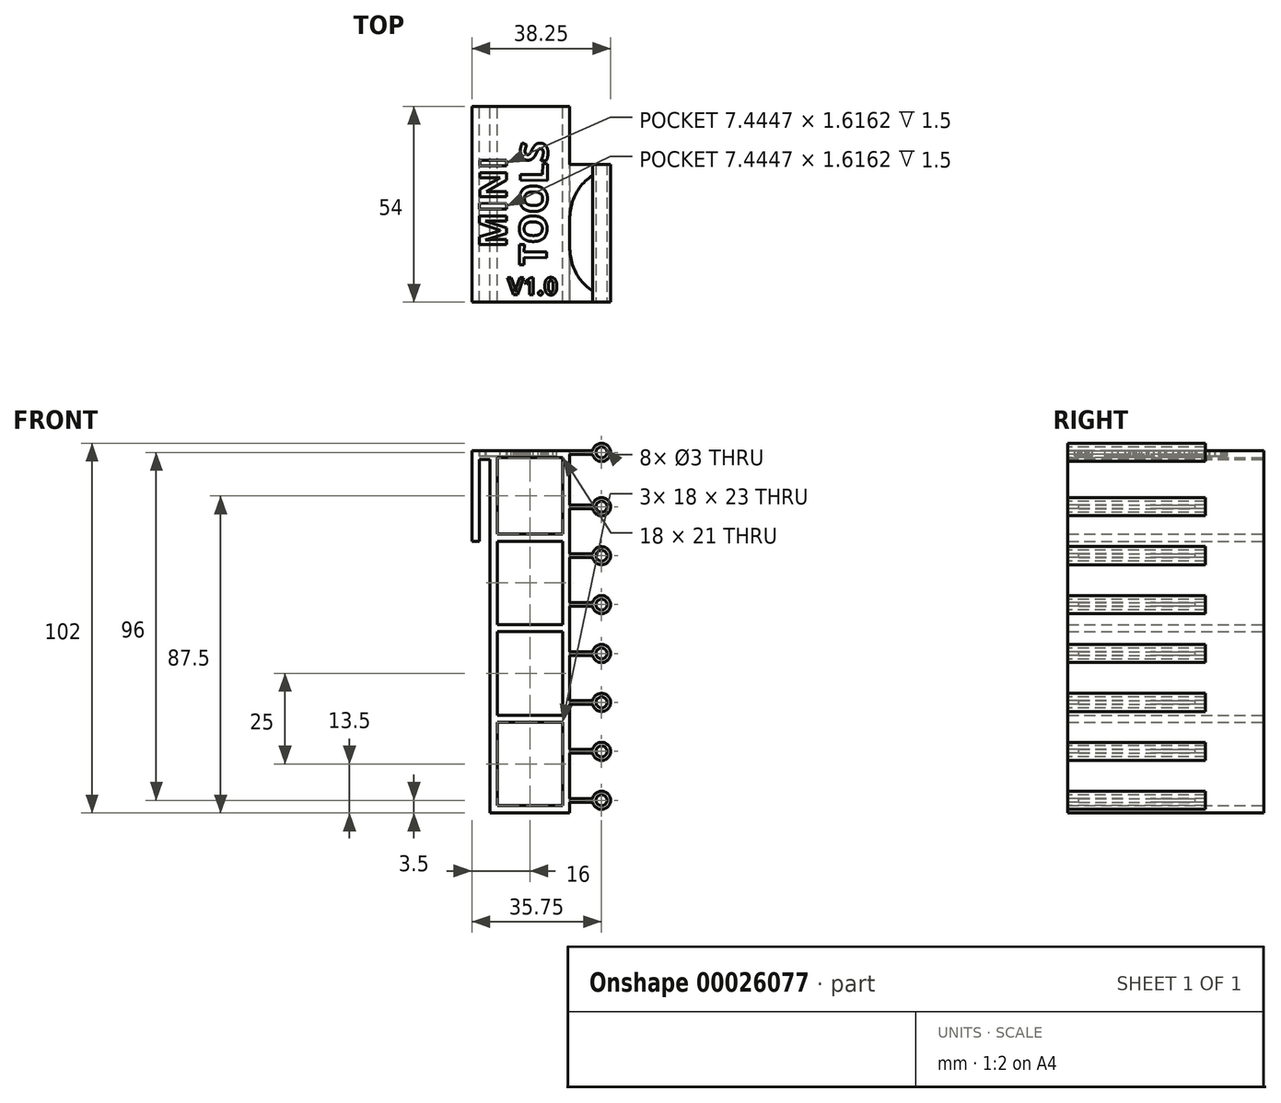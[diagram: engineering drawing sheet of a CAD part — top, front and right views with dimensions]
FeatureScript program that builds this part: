
annotation { "Feature Type Name" : "Feature", "Feature Type Description" : "" }
export const myFeature = defineFeature(function(context is Context, id is Id, definition is map)
    precondition{}
    {
        {
            var Q0;
            Q0=qCreatedBy(makeId("Front.planeOp"),FACE);
            var sketch = newSketch(context, id + "F0", { "sketchPlane" : qUnion([Q0])});
            skLineSegment(sketch, "E0", {"start": v(-37.92, 15.53) * mm, "end": v(-37.92, 40.53) * mm});
            skLineSegment(sketch, "E1", {"start": v(-37.92, 40.53) * mm, "end": v(-35.92, 40.53) * mm});
            skLineSegment(sketch, "E2", {"start": v(-35.92, 40.53) * mm, "end": v(-35.92, 15.53) * mm});
            skLineSegment(sketch, "E3", {"start": v(-35.92, 15.53) * mm, "end": v(-37.92, 15.53) * mm});
            skLineSegment(sketch, "E4", {"start": v(-35.92, 40.53) * mm, "end": v(-32.92, 40.53) * mm});
            skLineSegment(sketch, "E5", {"start": v(-32.92, 40.53) * mm, "end": v(-32.92, -59.47) * mm});
            skLineSegment(sketch, "E6", {"start": v(-32.92, -59.47) * mm, "end": v(-30.92, -59.47) * mm});
            skLineSegment(sketch, "E7", {"start": v(-30.92, -59.47) * mm, "end": v(-30.92, 40.53) * mm});
            skLineSegment(sketch, "E8", {"start": v(-30.92, 40.53) * mm, "end": v(-32.92, 40.53) * mm});
            skLineSegment(sketch, "E9", {"start": v(-30.92, -57.47) * mm, "end": v(-10.92, -57.47) * mm});
            skLineSegment(sketch, "E10", {"start": v(-10.92, -57.47) * mm, "end": v(-10.92, -59.47) * mm});
            skLineSegment(sketch, "E11", {"start": v(-10.92, -59.47) * mm, "end": v(-30.92, -59.47) * mm});
            skLineSegment(sketch, "E12", {"start": v(-35.92, 38.03) * mm, "end": v(-32.92, 38.03) * mm});
            skLineSegment(sketch, "E13", {"start": v(-10.92, -57.47) * mm, "end": v(-10.92, -34.47) * mm});
            skLineSegment(sketch, "E14", {"start": v(-10.92, -34.47) * mm, "end": v(-12.92, -34.47) * mm});
            skLineSegment(sketch, "E15", {"start": v(-12.92, -34.47) * mm, "end": v(-12.92, -57.47) * mm});
            skLineSegment(sketch, "E16.0.1.0", {"start": v(-30.92, -32.47) * mm, "end": v(-10.92, -32.47) * mm});
            skLineSegment(sketch, "E16.0.1.1", {"start": v(-10.92, -34.47) * mm, "end": v(-30.92, -34.47) * mm});
            skLineSegment(sketch, "E16.0.1.2", {"start": v(-10.92, -32.47) * mm, "end": v(-10.92, -34.47) * mm});
            skLineSegment(sketch, "E16.0.1.3", {"start": v(-10.92, -32.47) * mm, "end": v(-10.92, -9.47) * mm});
            skLineSegment(sketch, "E16.0.1.4", {"start": v(-10.92, -9.47) * mm, "end": v(-12.92, -9.47) * mm});
            skLineSegment(sketch, "E16.0.1.5", {"start": v(-12.92, -9.47) * mm, "end": v(-12.92, -32.47) * mm});
            skLineSegment(sketch, "E16.direction1", {"start": v(-30.92, -57.47) * mm, "end": v(-5.92, -57.47) * mm, "construction": true});
            skLineSegment(sketch, "E16.direction2", {"start": v(-30.92, -57.47) * mm, "end": v(-30.92, -32.47) * mm, "construction": true});
            skLineSegment(sketch, "E17.0.0.2", {"start": v(-30.92, -7.47) * mm, "end": v(-10.92, -7.47) * mm});
            skLineSegment(sketch, "E17.3.0.2", {"start": v(-10.92, -9.47) * mm, "end": v(-30.92, -9.47) * mm});
            skLineSegment(sketch, "E17.6.0.2", {"start": v(-10.92, -7.47) * mm, "end": v(-10.92, -9.47) * mm});
            skLineSegment(sketch, "E17.9.0.2", {"start": v(-10.92, -7.47) * mm, "end": v(-10.92, 15.53) * mm});
            skLineSegment(sketch, "E17.12.0.2", {"start": v(-10.92, 15.53) * mm, "end": v(-12.92, 15.53) * mm});
            skLineSegment(sketch, "E17.15.0.2", {"start": v(-12.92, 15.53) * mm, "end": v(-12.92, -7.47) * mm});
            skLineSegment(sketch, "E17.0.0.3", {"start": v(-30.92, 17.53) * mm, "end": v(-10.92, 17.53) * mm});
            skLineSegment(sketch, "E17.3.0.3", {"start": v(-10.92, 15.53) * mm, "end": v(-30.92, 15.53) * mm});
            skLineSegment(sketch, "E17.6.0.3", {"start": v(-10.92, 17.53) * mm, "end": v(-10.92, 15.53) * mm});
            skLineSegment(sketch, "E17.9.0.3", {"start": v(-10.92, 17.53) * mm, "end": v(-10.92, 40.53) * mm});
            skLineSegment(sketch, "E17.12.0.3", {"start": v(-10.92, 40.53) * mm, "end": v(-12.92, 40.53) * mm});
            skLineSegment(sketch, "E17.15.0.3", {"start": v(-12.92, 40.53) * mm, "end": v(-12.92, 17.53) * mm});
            skSolve(sketch);
        }
        {
            var Q0;
            Q0 = qSketchRegion(id + "F0", true);
            extrude(context, id + "F1", {"entities" : qUnion([Q0]), "depth" : 54 * mm});
        }
        {
            var Q0;
            Q0=makeQuery(id+"F1.opExtrude","CAP_FACE",FACE,{"disambiguationData":[OSD([sQuery(id+"F0.wireOp",EDGE,"E0"),sQuery(id+"F0.wireOp",EDGE,"E1"),sQuery(id+"F0.wireOp",EDGE,"E2"),sQuery(id+"F0.wireOp",EDGE,"E3"),sQuery(id+"F0.wireOp",EDGE,"E4"),sQuery(id+"F0.wireOp",EDGE,"E5"),sQuery(id+"F0.wireOp",EDGE,"E6"),sQuery(id+"F0.wireOp",EDGE,"E7"),sQuery(id+"F0.wireOp",EDGE,"E8"),sQuery(id+"F0.wireOp",EDGE,"E9"),sQuery(id+"F0.wireOp",EDGE,"E10"),sQuery(id+"F0.wireOp",EDGE,"E11"),sQuery(id+"F0.wireOp",EDGE,"E12"),sQuery(id+"F0.wireOp",EDGE,"E13"),sQuery(id+"F0.wireOp",EDGE,"E15"),sQuery(id+"F0.wireOp",EDGE,"E16.0.1.0"),sQuery(id+"F0.wireOp",EDGE,"E16.0.1.1"),sQuery(id+"F0.wireOp",EDGE,"E16.0.1.2"),sQuery(id+"F0.wireOp",EDGE,"E16.0.1.3"),sQuery(id+"F0.wireOp",EDGE,"E16.0.1.5"),sQuery(id+"F0.wireOp",EDGE,"E17.0.0.2"),sQuery(id+"F0.wireOp",EDGE,"E17.3.0.2"),sQuery(id+"F0.wireOp",EDGE,"E17.6.0.2"),sQuery(id+"F0.wireOp",EDGE,"E17.9.0.2"),sQuery(id+"F0.wireOp",EDGE,"E17.15.0.2"),sQuery(id+"F0.wireOp",EDGE,"E17.0.0.3"),sQuery(id+"F0.wireOp",EDGE,"E17.3.0.3"),sQuery(id+"F0.wireOp",EDGE,"E17.6.0.3"),sQuery(id+"F0.wireOp",EDGE,"E17.9.0.3"),sQuery(id+"F0.wireOp",EDGE,"E17.12.0.3"),sQuery(id+"F0.wireOp",EDGE,"E17.15.0.3")])],"isStart":false});
            var sketch = newSketch(context, id + "F2", { "sketchPlane" : qUnion([Q0])});
            skLineSegment(sketch, "E18.bottom", {"start": v(-10.92, 40.53) * mm, "end": v(-4.62, 40.53) * mm});
            skLineSegment(sketch, "E18.top", {"start": v(-10.92, 39.53) * mm, "end": v(-4.62, 39.53) * mm});
            skLineSegment(sketch, "E18.left", {"start": v(-10.92, 40.53) * mm, "end": v(-10.92, 39.53) * mm});
            skCircle(sketch, "E19", {"center": v(-5.22, 33.07) * mm, "radius": 5.5 * mm, "construction": true});
            skCircle(sketch, "E20", {"center": v(-5.72, 18.75) * mm, "radius": 5 * mm, "construction": true});
            skCircle(sketch, "E21", {"center": v(-2.17, 40.03) * mm, "radius": 2.5 * mm});
            skCircle(sketch, "E22", {"center": v(-2.17, 40.03) * mm, "radius": 1.5 * mm});
            skPoint(sketch, "E23.orphan", {"position": v(-2.17, 40.53) * mm});
            skPoint(sketch, "E24.orphan", {"position": v(-2.17, 39.53) * mm});
            skCircle(sketch, "E25.0.1.0", {"center": v(-2.17, 25.03) * mm, "radius": 1.5 * mm});
            skCircle(sketch, "E25.0.1.1", {"center": v(-2.17, 25.03) * mm, "radius": 2.5 * mm});
            skLineSegment(sketch, "E25.0.1.2", {"start": v(-10.92, 25.53) * mm, "end": v(-4.62, 25.53) * mm});
            skLineSegment(sketch, "E25.0.1.3", {"start": v(-10.92, 24.53) * mm, "end": v(-4.62, 24.53) * mm});
            skLineSegment(sketch, "E25.direction1", {"start": v(-2.17, 40.03) * mm, "end": v(22.83, 40.03) * mm, "construction": true});
            skLineSegment(sketch, "E25.direction2", {"start": v(-2.17, 40.03) * mm, "end": v(-2.17, 25.03) * mm, "construction": true});
            skLineSegment(sketch, "E26", {"start": v(-10.72, 24.53) * mm, "end": v(-10.72, 5.3) * mm, "construction": true});
            skLineSegment(sketch, "E27", {"start": v(-10.92, 24.53) * mm, "end": v(-10.92, 5.27) * mm, "construction": true});
            skLineSegment(sketch, "E28.0.1.0", {"start": v(-10.92, 11.03) * mm, "end": v(-4.62, 11.03) * mm});
            skLineSegment(sketch, "E28.0.1.1", {"start": v(-10.92, 12.03) * mm, "end": v(-4.62, 12.03) * mm});
            skCircle(sketch, "E28.0.1.2", {"center": v(-2.17, 11.53) * mm, "radius": 2.5 * mm});
            skLineSegment(sketch, "E28.0.2.0", {"start": v(-10.92, -2.47) * mm, "end": v(-4.62, -2.47) * mm});
            skLineSegment(sketch, "E28.0.2.1", {"start": v(-10.92, -1.47) * mm, "end": v(-4.62, -1.47) * mm});
            skCircle(sketch, "E28.0.2.2", {"center": v(-2.17, -1.97) * mm, "radius": 2.5 * mm});
            skLineSegment(sketch, "E28.0.3.0", {"start": v(-10.92, -15.97) * mm, "end": v(-4.62, -15.97) * mm});
            skLineSegment(sketch, "E28.0.3.1", {"start": v(-10.92, -14.97) * mm, "end": v(-4.62, -14.97) * mm});
            skCircle(sketch, "E28.0.3.2", {"center": v(-2.17, -15.47) * mm, "radius": 2.5 * mm});
            skLineSegment(sketch, "E28.direction1", {"start": v(-10.92, 24.53) * mm, "end": v(14.08, 24.53) * mm, "construction": true});
            skLineSegment(sketch, "E28.direction2", {"start": v(-10.92, 24.53) * mm, "end": v(-10.92, 11.03) * mm, "construction": true});
            skLineSegment(sketch, "E29.0.0.4", {"start": v(-10.92, -29.47) * mm, "end": v(-4.62, -29.47) * mm});
            skLineSegment(sketch, "E29.3.0.4", {"start": v(-10.92, -28.47) * mm, "end": v(-4.62, -28.47) * mm});
            skCircle(sketch, "E29.6.0.4", {"center": v(-2.17, -28.97) * mm, "radius": 2.5 * mm});
            skLineSegment(sketch, "E30.0.0.5", {"start": v(-10.92, -42.97) * mm, "end": v(-4.62, -42.97) * mm});
            skLineSegment(sketch, "E30.3.0.5", {"start": v(-10.92, -41.97) * mm, "end": v(-4.62, -41.97) * mm});
            skCircle(sketch, "E30.6.0.5", {"center": v(-2.17, -42.47) * mm, "radius": 2.5 * mm});
            skLineSegment(sketch, "E30.0.0.6", {"start": v(-10.92, -56.47) * mm, "end": v(-4.62, -56.47) * mm});
            skLineSegment(sketch, "E30.3.0.6", {"start": v(-10.92, -55.47) * mm, "end": v(-4.62, -55.47) * mm});
            skCircle(sketch, "E30.6.0.6", {"center": v(-2.17, -55.97) * mm, "radius": 2.5 * mm});
            skCircle(sketch, "E31.0.1.0", {"center": v(-2.17, 11.53) * mm, "radius": 1.5 * mm});
            skCircle(sketch, "E31.0.2.0", {"center": v(-2.17, -1.97) * mm, "radius": 1.5 * mm});
            skCircle(sketch, "E31.0.3.0", {"center": v(-2.17, -15.47) * mm, "radius": 1.5 * mm});
            skCircle(sketch, "E31.0.4.0", {"center": v(-2.17, -28.97) * mm, "radius": 1.5 * mm});
            skCircle(sketch, "E31.0.5.0", {"center": v(-2.17, -42.47) * mm, "radius": 1.5 * mm});
            skCircle(sketch, "E31.0.6.0", {"center": v(-2.17, -55.97) * mm, "radius": 1.5 * mm});
            skLineSegment(sketch, "E31.direction1", {"start": v(-2.17, 25.03) * mm, "end": v(22.83, 25.03) * mm, "construction": true});
            skLineSegment(sketch, "E31.direction2", {"start": v(-2.17, 25.03) * mm, "end": v(-2.17, 11.53) * mm, "construction": true});
            skSolve(sketch);
        }
        {
            var Q0;
            Q0 = qSketchRegion(id + "F2", true);
            var Q1;
            {var subQ2=sQuery(id+"F2.wireOp",EDGE,"E25.0.1.2");Q1=makeQuery(id+"F2.imprint","IMPRINT",FACE,{"disambiguationData":[TD([[makeQuery(id+"F2.imprint","IMPRINT",EDGE,{"derivedFrom":subQ2}),-1.0]])]});}
            var Q2;
            {var subQ2=sQuery(id+"F2.wireOp",EDGE,"E28.0.1.0");Q2=makeQuery(id+"F2.imprint","IMPRINT",FACE,{"disambiguationData":[TD([[makeQuery(id+"F2.imprint","IMPRINT",EDGE,{"derivedFrom":subQ2}),1.0]])]});}
            var Q3;
            {var subQ2=sQuery(id+"F2.wireOp",EDGE,"E28.0.2.0");Q3=makeQuery(id+"F2.imprint","IMPRINT",FACE,{"disambiguationData":[TD([[makeQuery(id+"F2.imprint","IMPRINT",EDGE,{"derivedFrom":subQ2}),1.0]])]});}
            var Q4;
            {var subQ2=sQuery(id+"F2.wireOp",EDGE,"E28.0.3.0");Q4=makeQuery(id+"F2.imprint","IMPRINT",FACE,{"disambiguationData":[TD([[makeQuery(id+"F2.imprint","IMPRINT",EDGE,{"derivedFrom":subQ2}),1.0]])]});}
            var Q5;
            {var subQ2=sQuery(id+"F2.wireOp",EDGE,"E29.0.0.4");Q5=makeQuery(id+"F2.imprint","IMPRINT",FACE,{"disambiguationData":[TD([[makeQuery(id+"F2.imprint","IMPRINT",EDGE,{"derivedFrom":subQ2}),1.0]])]});}
            var Q6;
            {var subQ2=sQuery(id+"F2.wireOp",EDGE,"E30.0.0.5");Q6=makeQuery(id+"F2.imprint","IMPRINT",FACE,{"disambiguationData":[TD([[makeQuery(id+"F2.imprint","IMPRINT",EDGE,{"derivedFrom":subQ2}),1.0]])]});}
            var Q7;
            {var subQ2=sQuery(id+"F2.wireOp",EDGE,"E30.0.0.6");Q7=makeQuery(id+"F2.imprint","IMPRINT",FACE,{"disambiguationData":[TD([[makeQuery(id+"F2.imprint","IMPRINT",EDGE,{"derivedFrom":subQ2}),1.0]])]});}
            extrude(context, id + "F3", {"entities" : qUnion([Q0, Q1, Q2, Q3, Q4, Q5, Q6, Q7]), "oppositeDirection" : true, "depth" : 38 * mm});
        }
        {
            var Q0;
            Q0=makeQuery(id+"F3.opExtrude","SWEPT_BODY",BODY,{"disambiguationData":[OSD([sQuery(id+"F0.wireOp",EDGE,"E10"),sQuery(id+"F0.wireOp",EDGE,"E13"),sQuery(id+"F0.wireOp",EDGE,"E16.0.1.2"),sQuery(id+"F0.wireOp",EDGE,"E16.0.1.3"),sQuery(id+"F0.wireOp",EDGE,"E17.6.0.2"),sQuery(id+"F0.wireOp",EDGE,"E17.9.0.2"),sQuery(id+"F0.wireOp",EDGE,"E17.6.0.3"),sQuery(id+"F0.wireOp",EDGE,"E17.9.0.3"),sQuery(id+"F2.wireOp",EDGE,"E30.0.0.6"),sQuery(id+"F2.wireOp",EDGE,"E30.3.0.6"),sQuery(id+"F2.wireOp",EDGE,"E30.6.0.6"),sQuery(id+"F2.wireOp",EDGE,"E31.0.6.0")])]});
            var Q1;
            Q1=makeQuery(id+"F3.opExtrude","SWEPT_BODY",BODY,{"disambiguationData":[OSD([sQuery(id+"F0.wireOp",EDGE,"E10"),sQuery(id+"F0.wireOp",EDGE,"E13"),sQuery(id+"F0.wireOp",EDGE,"E16.0.1.2"),sQuery(id+"F0.wireOp",EDGE,"E16.0.1.3"),sQuery(id+"F0.wireOp",EDGE,"E17.6.0.2"),sQuery(id+"F0.wireOp",EDGE,"E17.9.0.2"),sQuery(id+"F0.wireOp",EDGE,"E17.6.0.3"),sQuery(id+"F0.wireOp",EDGE,"E17.9.0.3"),sQuery(id+"F2.wireOp",EDGE,"E30.0.0.5"),sQuery(id+"F2.wireOp",EDGE,"E30.3.0.5"),sQuery(id+"F2.wireOp",EDGE,"E30.6.0.5"),sQuery(id+"F2.wireOp",EDGE,"E31.0.5.0")])]});
            var Q2;
            Q2=makeQuery(id+"F3.opExtrude","SWEPT_BODY",BODY,{"disambiguationData":[OSD([sQuery(id+"F0.wireOp",EDGE,"E10"),sQuery(id+"F0.wireOp",EDGE,"E13"),sQuery(id+"F0.wireOp",EDGE,"E16.0.1.2"),sQuery(id+"F0.wireOp",EDGE,"E16.0.1.3"),sQuery(id+"F0.wireOp",EDGE,"E17.6.0.2"),sQuery(id+"F0.wireOp",EDGE,"E17.9.0.2"),sQuery(id+"F0.wireOp",EDGE,"E17.6.0.3"),sQuery(id+"F0.wireOp",EDGE,"E17.9.0.3"),sQuery(id+"F2.wireOp",EDGE,"E29.0.0.4"),sQuery(id+"F2.wireOp",EDGE,"E29.3.0.4"),sQuery(id+"F2.wireOp",EDGE,"E29.6.0.4"),sQuery(id+"F2.wireOp",EDGE,"E31.0.4.0")])]});
            var Q3;
            Q3=makeQuery(id+"F3.opExtrude","SWEPT_BODY",BODY,{"disambiguationData":[OSD([sQuery(id+"F0.wireOp",EDGE,"E10"),sQuery(id+"F0.wireOp",EDGE,"E13"),sQuery(id+"F0.wireOp",EDGE,"E16.0.1.2"),sQuery(id+"F0.wireOp",EDGE,"E16.0.1.3"),sQuery(id+"F0.wireOp",EDGE,"E17.6.0.2"),sQuery(id+"F0.wireOp",EDGE,"E17.9.0.2"),sQuery(id+"F0.wireOp",EDGE,"E17.6.0.3"),sQuery(id+"F0.wireOp",EDGE,"E17.9.0.3"),sQuery(id+"F2.wireOp",EDGE,"E28.0.3.0"),sQuery(id+"F2.wireOp",EDGE,"E28.0.3.1"),sQuery(id+"F2.wireOp",EDGE,"E28.0.3.2"),sQuery(id+"F2.wireOp",EDGE,"E31.0.3.0")])]});
            var Q4;
            Q4=makeQuery(id+"F3.opExtrude","SWEPT_BODY",BODY,{"disambiguationData":[OSD([sQuery(id+"F0.wireOp",EDGE,"E10"),sQuery(id+"F0.wireOp",EDGE,"E13"),sQuery(id+"F0.wireOp",EDGE,"E16.0.1.2"),sQuery(id+"F0.wireOp",EDGE,"E16.0.1.3"),sQuery(id+"F0.wireOp",EDGE,"E17.6.0.2"),sQuery(id+"F0.wireOp",EDGE,"E17.9.0.2"),sQuery(id+"F0.wireOp",EDGE,"E17.6.0.3"),sQuery(id+"F0.wireOp",EDGE,"E17.9.0.3"),sQuery(id+"F2.wireOp",EDGE,"E28.0.2.0"),sQuery(id+"F2.wireOp",EDGE,"E28.0.2.1"),sQuery(id+"F2.wireOp",EDGE,"E28.0.2.2"),sQuery(id+"F2.wireOp",EDGE,"E31.0.2.0")])]});
            var Q5;
            Q5=makeQuery(id+"F3.opExtrude","SWEPT_BODY",BODY,{"disambiguationData":[OSD([sQuery(id+"F0.wireOp",EDGE,"E10"),sQuery(id+"F0.wireOp",EDGE,"E13"),sQuery(id+"F0.wireOp",EDGE,"E16.0.1.2"),sQuery(id+"F0.wireOp",EDGE,"E16.0.1.3"),sQuery(id+"F0.wireOp",EDGE,"E17.6.0.2"),sQuery(id+"F0.wireOp",EDGE,"E17.9.0.2"),sQuery(id+"F0.wireOp",EDGE,"E17.6.0.3"),sQuery(id+"F0.wireOp",EDGE,"E17.9.0.3"),sQuery(id+"F2.wireOp",EDGE,"E28.0.1.0"),sQuery(id+"F2.wireOp",EDGE,"E28.0.1.1"),sQuery(id+"F2.wireOp",EDGE,"E28.0.1.2"),sQuery(id+"F2.wireOp",EDGE,"E31.0.1.0")])]});
            var Q6;
            Q6=makeQuery(id+"F3.opExtrude","SWEPT_BODY",BODY,{"disambiguationData":[OSD([sQuery(id+"F0.wireOp",EDGE,"E10"),sQuery(id+"F0.wireOp",EDGE,"E13"),sQuery(id+"F0.wireOp",EDGE,"E16.0.1.2"),sQuery(id+"F0.wireOp",EDGE,"E16.0.1.3"),sQuery(id+"F0.wireOp",EDGE,"E17.6.0.2"),sQuery(id+"F0.wireOp",EDGE,"E17.9.0.2"),sQuery(id+"F0.wireOp",EDGE,"E17.6.0.3"),sQuery(id+"F0.wireOp",EDGE,"E17.9.0.3"),sQuery(id+"F2.wireOp",EDGE,"E25.0.1.0"),sQuery(id+"F2.wireOp",EDGE,"E25.0.1.1"),sQuery(id+"F2.wireOp",EDGE,"E25.0.1.2"),sQuery(id+"F2.wireOp",EDGE,"E25.0.1.3")])]});
            var Q7;
            Q7=makeQuery(id+"F3.opExtrude","SWEPT_BODY",BODY,{"disambiguationData":[OSD([sQuery(id+"F2.wireOp",EDGE,"E18.bottom"),sQuery(id+"F2.wireOp",EDGE,"E18.top"),sQuery(id+"F2.wireOp",EDGE,"E18.left"),sQuery(id+"F2.wireOp",EDGE,"E21"),sQuery(id+"F2.wireOp",EDGE,"E22")])]});
            var Q8;
            Q8=makeQuery(id+"F1.opExtrude","SWEPT_BODY",BODY,{"disambiguationData":[OSD([sQuery(id+"F0.wireOp",EDGE,"E0"),sQuery(id+"F0.wireOp",EDGE,"E1"),sQuery(id+"F0.wireOp",EDGE,"E2"),sQuery(id+"F0.wireOp",EDGE,"E3"),sQuery(id+"F0.wireOp",EDGE,"E4"),sQuery(id+"F0.wireOp",EDGE,"E5"),sQuery(id+"F0.wireOp",EDGE,"E6"),sQuery(id+"F0.wireOp",EDGE,"E7"),sQuery(id+"F0.wireOp",EDGE,"E8"),sQuery(id+"F0.wireOp",EDGE,"E9"),sQuery(id+"F0.wireOp",EDGE,"E10"),sQuery(id+"F0.wireOp",EDGE,"E11"),sQuery(id+"F0.wireOp",EDGE,"E12"),sQuery(id+"F0.wireOp",EDGE,"E13"),sQuery(id+"F0.wireOp",EDGE,"E15"),sQuery(id+"F0.wireOp",EDGE,"E16.0.1.0"),sQuery(id+"F0.wireOp",EDGE,"E16.0.1.1"),sQuery(id+"F0.wireOp",EDGE,"E16.0.1.2"),sQuery(id+"F0.wireOp",EDGE,"E16.0.1.3"),sQuery(id+"F0.wireOp",EDGE,"E16.0.1.5"),sQuery(id+"F0.wireOp",EDGE,"E17.0.0.2"),sQuery(id+"F0.wireOp",EDGE,"E17.3.0.2"),sQuery(id+"F0.wireOp",EDGE,"E17.6.0.2"),sQuery(id+"F0.wireOp",EDGE,"E17.9.0.2"),sQuery(id+"F0.wireOp",EDGE,"E17.15.0.2"),sQuery(id+"F0.wireOp",EDGE,"E17.0.0.3"),sQuery(id+"F0.wireOp",EDGE,"E17.3.0.3"),sQuery(id+"F0.wireOp",EDGE,"E17.6.0.3"),sQuery(id+"F0.wireOp",EDGE,"E17.9.0.3"),sQuery(id+"F0.wireOp",EDGE,"E17.12.0.3"),sQuery(id+"F0.wireOp",EDGE,"E17.15.0.3")])]});
            booleanBodies(context, id + "F4", {"operationType" : BooleanOperationType.UNION, "tools" : qUnion([Q0, Q1, Q2, Q3, Q4, Q5, Q6, Q7, Q8])});
        }
        {
            var Q0;
            Q0=makeQuery(id+"F4.opBoolean","MERGE",FACE,{"derivedFrom":[makeQuery(id+"F1.opExtrude","SWEPT_FACE",FACE,{"disambiguationData":[OSD([sQuery(id+"F0.wireOp",EDGE,"E17.12.0.3")])]}),makeQuery(id+"F3.opExtrude","SWEPT_FACE",FACE,{"disambiguationData":[OSD([sQuery(id+"F2.wireOp",EDGE,"E18.bottom")])]})]});
            var sketch = newSketch(context, id + "F5", { "sketchPlane" : qUnion([Q0])});
            skLineSegment(sketch, "E32", {"start": v(-10.92, -16) * mm, "end": v(-10.92, -54) * mm, "construction": true});
            skLineSegment(sketch, "E33.bottom", {"start": v(-10.92, -51) * mm, "end": v(-4.62, -51) * mm});
            skLineSegment(sketch, "E33.top", {"start": v(-10.92, -19) * mm, "end": v(-4.62, -19) * mm});
            skLineSegment(sketch, "E33.left", {"start": v(-10.92, -51) * mm, "end": v(-10.92, -19) * mm});
            skLineSegment(sketch, "E33.right", {"start": v(-4.62, -51) * mm, "end": v(-4.62, -19) * mm});
            skSolve(sketch);
        }
        {
            var Q0;
            Q0 = qSketchRegion(id + "F5", true);
            extrude(context, id + "F6", {"entities" : qUnion([Q0]), "operationType" : NewBodyOperationType.REMOVE, "oppositeDirection" : true, "depth" : 300 * mm});
        }
        {
            var Q0;
            Q0=makeQuery(id+"F6.boolean.opBoolean","COPY",EDGE,{"derivedFrom":makeQuery(id+"F6.opExtrude","SWEPT_EDGE",EDGE,{"disambiguationData":[OSD([sQuery(id+"F5.wireOp",EDGE,"E33.top"),sQuery(id+"F5.wireOp",EDGE,"E33.left")])]})});
            var Q1;
            Q1=makeQuery(id+"F6.boolean.opBoolean","COPY",EDGE,{"derivedFrom":makeQuery(id+"F6.opExtrude","SWEPT_EDGE",EDGE,{"disambiguationData":[OSD([sQuery(id+"F5.wireOp",EDGE,"E33.bottom"),sQuery(id+"F5.wireOp",EDGE,"E33.left")])]})});
            fillet(context, id + "F7", {"entities" : qUnion([Q0, Q1]), "radius" : 15 * mm, "tangentPropagation" : true, "rho" : 0.5, "crossSection" : FilletCrossSection.CONIC, "allowEdgeOverflow" : false});
        }
        {
            var Q0;
            {var subQ0=sQuery(id+"F0.wireOp",EDGE,"E7");Q0=makeQuery(id+"F1.opExtrude","SWEPT_FACE",FACE,{"disambiguationData":[OSD([subQ0]),TDD([makeQuery(id+"F0.imprint","IMPRINT",EDGE,{"disambiguationData":[TD([[makeQuery(id+"F0.imprint","INTERSECT",VERTEX,{"derivedFrom":[subQ0,sQuery(id+"F0.wireOp",EDGE,"E8")]}),1.0]])],"derivedFrom":subQ0})])]});}
            var sketch = newSketch(context, id + "F8", { "sketchPlane" : qUnion([Q0])});
            skLineSegment(sketch, "E34.bottom", {"start": v(-54, 40.53) * mm, "end": v(0, 40.53) * mm});
            skLineSegment(sketch, "E34.top", {"start": v(-54, 38.53) * mm, "end": v(0, 38.53) * mm});
            skLineSegment(sketch, "E34.left", {"start": v(-54, 40.53) * mm, "end": v(-54, 38.53) * mm});
            skLineSegment(sketch, "E34.right", {"start": v(0, 40.53) * mm, "end": v(0, 38.53) * mm});
            skSolve(sketch);
        }
        {
            var Q0;
            Q0 = qSketchRegion(id + "F8", true);
            extrude(context, id + "F9", {"entities" : qUnion([Q0]), "operationType" : NewBodyOperationType.ADD, "depth" : 18 * mm});
        }
        {
            var Q0;
            Q0=makeQuery(id+"F9.boolean.opBoolean","MERGE",FACE,{"derivedFrom":[makeQuery(id+"F1.opExtrude","SWEPT_FACE",FACE,{"disambiguationData":[OSD([sQuery(id+"F0.wireOp",EDGE,"E1"),sQuery(id+"F0.wireOp",EDGE,"E4"),sQuery(id+"F0.wireOp",EDGE,"E8")])]}),makeQuery(id+"F4.opBoolean","MERGE",FACE,{"derivedFrom":[makeQuery(id+"F1.opExtrude","SWEPT_FACE",FACE,{"disambiguationData":[OSD([sQuery(id+"F0.wireOp",EDGE,"E17.12.0.3")])]}),makeQuery(id+"F3.opExtrude","SWEPT_FACE",FACE,{"disambiguationData":[OSD([sQuery(id+"F2.wireOp",EDGE,"E18.bottom")])]})]}),makeQuery(id+"F9.opExtrude","SWEPT_FACE",FACE,{"disambiguationData":[OSD([sQuery(id+"F8.wireOp",EDGE,"E34.bottom")])]})]});
            var sketch = newSketch(context, id + "F10", { "sketchPlane" : qUnion([Q0])});
            skText(sketch, "E35", { "text": "MINI", "fontName": "OpenSans-Bold.ttf"});
            skText(sketch, "E36", { "text": "TOOLS", "fontName": "OpenSans-Bold.ttf"});
            skLineSegment(sketch, "E37", {"start": v(-37.92, -27) * mm, "end": v(-11.48, -27) * mm, "construction": true});
            skText(sketch, "E38", { "text": "V1.0", "fontName": "OpenSans-Bold.ttf"});
            skLineSegment(sketch, "E39", {"start": v(-21.27, -54) * mm, "end": v(-21.27, -46.75) * mm, "construction": true});
            const initialGuessF10  = {"E35": [-0.02843, -0.03913, 0.00525, 0.99999, 0.0075], "E36": [-0.0174, -0.044, 0.0118, 0.99993, 0.0075], "E38": [-0.02804, -0.05201, 1, 0, 0.00478]};
            skSetInitialGuess(sketch, initialGuessF10);
            skSolve(sketch);
        }
        {
            var Q0;
            Q0 = qSketchRegion(id + "F10", true);
            extrude(context, id + "F11", {"entities" : qUnion([Q0]), "operationType" : NewBodyOperationType.REMOVE, "oppositeDirection" : true, "depth" : 1.5 * mm});
        }
    });
